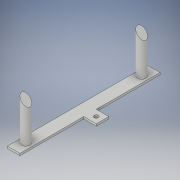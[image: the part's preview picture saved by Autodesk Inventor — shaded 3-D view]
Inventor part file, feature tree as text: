
AUTODESK INVENTOR PART (.ipt)
format: ipt  version: 2018 (Build 220112000, 112)  size: 141,312 bytes
history: native  units: in
note: dims shown in document units (in); Inventor stores cm internally (conversion verified against a paired STEP export)
features: extrude x4, sketch x4
ambient origin geometry x8: Origin, YZ Plane, XZ Plane, XY Plane, X Axis, Y Axis, Z Axis, Center Point
bodies: Solid1 (feature_tree)
feature tree (8):
  extrude  "Extrusion1"  Depth=0.4724in
  extrude  "Extrusion2"  Depth=0.2362in
  extrude  "Extrusion3"  Depth=2.6378in
  extrude  "Extrusion4"  Depth=0.0787in
  sketch  "Sketch1"  dims[d0=0.2362in d1=0.4724in]
  sketch  "Sketch2"  dims[d2=0.1181in d3=0.2362in]
  sketch  "Sketch3"  dims[d4=2.6378in d5=2.1811in]
  sketch  "Sketch4"  dims[d6=1.0906in d7=1.0906in d8=0.1575in d9=0.1575in d10=0.0394in d11=0.0in d12=2.1811in d13=1.0906in d14=1.0906in d15=0.1575in d16=0.1575in d17=0.7874in d18=0.0in d19=0.2756in d20=3.937in d21=0.0in d22=0.1181in d23=0.0787in d24=1.0in d25=0.0in]
